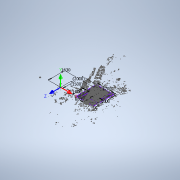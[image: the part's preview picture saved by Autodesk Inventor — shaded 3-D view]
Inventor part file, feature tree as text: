
AUTODESK INVENTOR PART (.ipt)
format: ipt  version: 2021 (Build 250183000, 183)  size: 3,832,320 bytes
history: native  units: mm
features: other x15, extrude x1, sketch x1, projected_geometry x1, surface_op x1
ambient origin geometry x8: Origin, YZ Plane, XZ Plane, XY Plane, X Axis, Y Axis, Z Axis, Center Point
bodies: Body1 (feature_tree)
feature tree (19):
  other  "leonOSM"
  other  "Sólido1"
  other  "SCU1"
  extrude  "Extrusión1"  Depth=1700000.0mm
  sketch  "Boceto1"  dims[d0=0.0mm d1=0.0mm d2=0.0mm d3=0.0mm d4=0.0mm d5=0.0mm d7=1700000.0mm d9=2000000.0mm d10=1000.0mm d11=0.0mm d14=1500000.0mm d15=2000000.0mm d17=1630000.0mm d18=1000000.0mm d19=850000.0mm]
  projected_geometry  "Contorno proyectado1"
  other  "BuildingEntrance"
  other  "Building"
  other  "Pool"
  other  "SoccerPitch"
  other  "RoadArea"
  surface_op  "SurfaceArea"
  other  "SCU1: Plano YZ"
  other  "SCU1: Plano XZ"
  other  "SCU1: Plano XY"
  other  "SCU1: Eje X"
  other  "SCU1: Eje Y"
  other  "SCU1: Eje Z"
  other  "SCU1: Centro"
